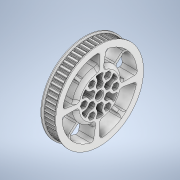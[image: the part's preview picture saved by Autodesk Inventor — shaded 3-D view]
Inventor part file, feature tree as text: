
AUTODESK INVENTOR PART (.ipt)
format: ipt  version: 2020 (Build 240168000, 168)  size: 4,062,208 bytes
history: native  units: mm
features: thicken_offset x25, extrude x20, sketch x20, projected_geometry x19, pattern_circular x10, fillet x7, chamfer x5, plane x4, other x4, reference x1
ambient origin geometry x8: Origin, YZ Plane, XZ Plane, XY Plane, X Axis, Y Axis, Z Axis, Center Point
bodies: Solid1 (feature_tree)
feature tree (115):
  plane  "Work Plane1"
  extrude  "Extrusion1"  Depth=110.0mm
  plane  "Work Plane2"
  extrude  "Extrusion2"  [1 undecoded]
  extrude  "Extrusion3"  Depth=20.0mm TaperAngle=0.0deg
  thicken_offset  "Thicken1"
  extrude  "Extrusion4"  Depth=10.0mm
  extrude  "Extrusion5"  Depth=8.0mm TaperAngle=0.0deg
  extrude  "Extrusion6"  Depth=3.0mm TaperAngle=0.0deg
  thicken_offset  "Thicken9"
  thicken_offset  "Thicken10"
  extrude  "Extrusion20"  Depth=1.0mm
  chamfer  "Chamfer11"  Distance=7.0mm
  chamfer  "Chamfer12"  Distance=1.0mm Angle=45.0deg
  extrude  "Extrusion21"  Depth=2.0mm
  pattern_circular  "Circular Pattern6"  Count=6  [1 undecoded]
  extrude  "Extrusion22"  Depth=2.0mm
  pattern_circular  "Circular Pattern7"  Count=4  [1 undecoded]
  extrude  "Extrusion24"  Depth=7.0mm
  pattern_circular  "Circular Pattern11"  [2 undecoded]
  plane  "Work Plane3"
  extrude  "Extrusion25"  Depth=1.0mm
  extrude  "Extrusion26"  Depth=1.0mm
  thicken_offset  "Thicken14"
  thicken_offset  "Thicken15"
  pattern_circular  "Circular Pattern12"  Count=3  [1 undecoded]
  chamfer  "Chamfer13"  Distance=3.0mm
  fillet  "Fillet13"  Radius=60.0mm
  fillet  "Fillet14"  Radius=88.0mm
  chamfer  "Chamfer14"  Distance=44.0mm
  extrude  "Extrusion27"  Depth=1.0mm
  pattern_circular  "Circular Pattern13"  [2 undecoded]
  thicken_offset  "Thicken16"
  thicken_offset  "Thicken17"
  chamfer  "Chamfer15"  Distance=2.0mm
  thicken_offset  "Thicken18"
  thicken_offset  "Thicken19"
  thicken_offset  "Thicken20"
  thicken_offset  "Thicken21"
  plane  "Work Plane4"
  extrude  "Extrusion28"  Depth=2.0mm
  pattern_circular  "Circular Pattern14"  [2 undecoded]
  fillet  "Fillet17"  Radius=40.0mm
  fillet  "Fillet18"  Radius=2.0mm
  pattern_circular  "Circular Pattern15"  [2 undecoded]
  thicken_offset  "Thicken22"
  thicken_offset  "Thicken23"
  extrude  "Extrusion29"  Depth=3.0mm
  pattern_circular  "Circular Pattern16"  Angle=45.0deg  [1 undecoded]
  extrude  "Extrusion30"  Depth=1.0mm
  extrude  "Extrusion31"  Depth=1.0mm TaperAngle=360.0deg
  pattern_circular  "Circular Pattern17"  [2 undecoded]
  extrude  "Extrusion32"  Depth=1.0mm
  pattern_circular  "Circular Pattern18"  [2 undecoded]
  fillet  "Fillet19"  Radius=0.5mm
  fillet  "Fillet20"  Radius=2.0mm
  extrude  "Extrusion33"  Depth=1.0mm
  extrude  "Extrusion34"  Depth=1.0mm
  thicken_offset  "Thicken24"
  thicken_offset  "Thicken25"
  thicken_offset  "Thicken26"
  thicken_offset  "Thicken27"
  thicken_offset  "Thicken28"
  thicken_offset  "Thicken29"
  thicken_offset  "Thicken30"
  thicken_offset  "Thicken31"
  thicken_offset  "Thicken32"
  thicken_offset  "Thicken33"
  thicken_offset  "Thicken34"
  thicken_offset  "Thicken35"
  fillet  "Fillet22"  Radius=0.855mm
  sketch  "Sketch1"  dims[d0=0.0mm d1=110.0mm]
  sketch  "Sketch2"  dims[d2=10.0mm d3=0.0mm d4=-1.0mm]
  sketch  "Sketch3"  dims[d5=110.0mm d6=20.0mm d7=0.0mm]
  projected_geometry  "Projected Loop1"
  sketch  "Sketch4"  dims[d8=20.0mm d9=0.0mm d10=10.0mm d11=9.0mm]
  projected_geometry  "Projected Loop2"
  sketch  "Sketch5"  dims[d12=8.0mm d13=20.0mm d14=0.0mm]
  sketch  "Sketch6"  dims[d15=102.0mm d16=3.0mm d17=0.0mm]
  sketch  "Sketch26"  dims[d18=3.0mm d19=0.0mm d143=1.0mm]
  reference  "Reference6"
  sketch  "Sketch27"  dims[d144=1.0mm]
  projected_geometry  "Projected Loop18"
  sketch  "Sketch28"  dims[d145=1.0mm]
  projected_geometry  "Projected Loop19"
  sketch  "Sketch30"  dims[d146=1.0mm]
  projected_geometry  "Projected Loop21"
  sketch  "Sketch31"  dims[d216=50.0mm d217=7.0mm d218=0.0mm d219=1.0mm d220=2.0mm d221=45.0deg]
  projected_geometry  "Projected Loop22"
  sketch  "Sketch32"  dims[d222=1.5mm d223=2.0mm d224=45.0deg d225=18.0mm]
  projected_geometry  "Projected Loop23"
  projected_geometry  "Projected Loop24"
  sketch  "Sketch33"  dims[d226=4.2mm]
  sketch  "Sketch34"  dims[d227=7.0mm d228=0.0mm d229=60.0mm d230=62.831853mm]
  projected_geometry  "Projected Loop25"
  sketch  "Sketch35"  dims[d232=2.0mm d233=2.0mm]
  projected_geometry  "Projected Loop26"
  sketch  "Sketch36"  dims[d234=17.0mm d235=40.0mm]
  projected_geometry  "Projected Loop27"
  sketch  "Sketch37"  dims[d236=7.0mm d237=0.0mm d238=30.0mm d239=62.831853mm]
  projected_geometry  "Projected Loop28"
  projected_geometry  "Projected Loop29"
  sketch  "Sketch38"  dims[d256=16.0mm]
  projected_geometry  "Projected Loop30"
  projected_geometry  "Projected Loop31"
  projected_geometry  "Projected Loop32"
  projected_geometry  "Projected Loop33"
  sketch  "Sketch40"  dims[d257=13.0mm]
  projected_geometry  "Projected Loop34"
  sketch  "Sketch41"  dims[d259=13.0mm d261=7.0mm d262=0.0mm d264=4.2mm d265=4.2mm d266=30.0mm d267=62.831853mm d269=3.0mm d270=0.0mm d271=60.0mm d272=88.0mm d273=44.0mm d274=1.7mm d275=3.0mm d276=0.0mm d277=2.0mm d278=2.0mm d279=2.5mm d280=1.0mm d281=40.0mm d282=62.831853mm d284=4.0mm d285=2.0mm d286=45.0deg d287=3.0mm d288=3.0mm d291=1.0mm d292=2.0mm d293=45.0deg d294=4.05mm d295=60.0mm d297=360.0deg d299=4.0mm d300=0.0mm d301=60.0mm d302=62.831853mm d304=0.5mm d305=0.7mm d306=0.5mm d307=0.7mm d308=1.5mm d309=2.0mm d310=45.0deg d311=0.855mm d312=0.855mm d313=0.855mm d314=0.855mm d315=0.855mm d316=0.855mm d317=0.855mm d318=0.855mm d319=-4.0mm d320=3.0mm d321=25.0mm d322=85.71mm d323=55.0mm d324=10.0mm d325=0.0mm d326=40.0mm d327=62.831853mm d329=4.0mm d330=2.0mm d331=40.0mm d332=62.831853mm d334=0.025mm d335=0.05mm d336=0.075mm d337=0.075mm d338=15.0mm d339=43.0mm d340=2.0mm d341=2.0mm d342=10.0mm d343=0.0mm d344=30.0mm d345=62.831853mm d347=43.0mm d348=10.0mm d349=9.0mm d350=10.0mm d351=10.0mm d352=10.0mm d353=10.0mm d354=10.0mm d355=9.0mm d356=9.0mm d357=9.0mm d358=9.0mm d359=9.0mm d360=10.0mm d361=0.0mm d362=3.0mm d363=10.0mm d364=0.0mm d365=60.0mm d366=62.831853mm d368=3.0mm d369=3.0mm d370=10.0mm d371=0.0mm d372=30.0mm d373=62.831853mm d375=1.0mm d376=2.0mm d377=2.0mm d379=10.0mm d380=0.0mm d381=10.5mm d382=0.0mm d383=2.0mm d384=1.0mm d385=2.0mm d386=1.0mm d387=2.0mm d388=1.0mm d389=2.0mm d390=1.0mm d391=2.0mm d392=1.0mm d393=2.0mm d394=1.0mm d395=2.0mm d396=1.0mm d397=2.0mm d398=1.0mm d399=2.0mm d400=1.0mm d401=2.0mm d402=1.0mm d403=2.0mm d404=1.0mm d405=2.0mm d406=1.0mm d407=1.0mm]
  projected_geometry  "Projected Loop35"
  other  "_ATP60XL037-A-C12_b"
  parser-record x1  (decoder bookkeeping rows leaked as tree rows — omitted from the tree; the rows remain in map.json)
  other  "joint_base.iam"
  other  "bearing_6810zz:1"
note: 17 required parameter values undecoded (feature->parameter linkage not recoverable at this tier; creation-order binding heuristic only, values carry confidence <= 0.55)
note: 1 file-system path scrubbed to <path> (originals preserved in map.json)
